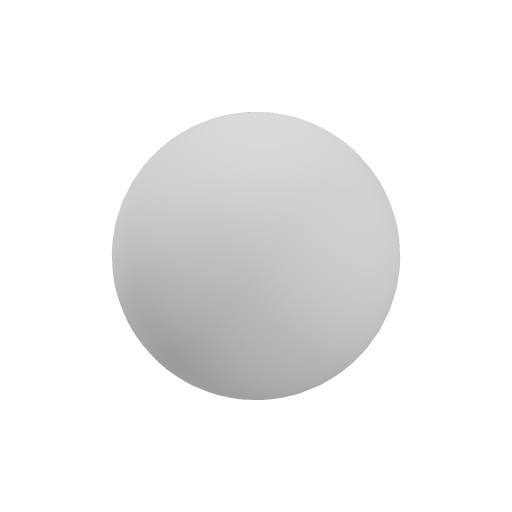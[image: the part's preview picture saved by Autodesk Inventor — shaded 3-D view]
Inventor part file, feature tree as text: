
AUTODESK INVENTOR PART (.ipt)
format: ipt  version: 2023 (Build 270158000, 158)  size: 120,832 bytes
history: native  units: in
note: dims shown in document units (in); Inventor stores cm internally (conversion verified against a paired STEP export)
features: revolve x1, sketch x1
ambient origin geometry x8: Origin, YZ Plane, XZ Plane, XY Plane, X Axis, Y Axis, Z Axis, Center Point
bodies: Solid1 (feature_tree)
feature tree (2):
  revolve  "Revolution1"  Angle=90.0deg
  sketch  "Sketch1"  dims[d0=3.0in d1=90.0deg]
